# Revit family: bfs-15_150ska2_tka2_60Hz
name_source: partatom
category: 機械設備
units: mm (PartAtom-declared; Revit-internal decimal feet)

## family parameters
OmniClass タイトル = Centrifugal Fans
OmniClass 番号 = 23.75.35.17.27
パーツ タイプ = 割り込み
ロード時にボイドで切り取り = いいえ
丸型コネクタ寸法 = 直径を使用
作業面ベース = いいえ
共有 = いいえ
常に垂直 = はい
部屋計算ポイント = はい

## types (13) — shared parameters
Clearance Left = 450  [stored 1.47638 ft]
IfcExportAs = IfcFanType
IfcExportType = CENTRIFUGALFORWARDCURVED
MID静圧 = 0.0 Pa
MID風量 = 0.0 m³/h
OmniClassCode = 23-33 31 19 13 15
URL = https://www.mitsubishielectric.co.jp
Uniclass2015Code = Pr_65_67_29_12
Uniclass2015Title = Centrifugal fans
Uniclass2015Version = Systems v1.9
サービススペース = はい
ファンの種類 = 多翼形
仕様書バージョン = Version1.0
企業コード = 108420
分類コード = 50052502100020
周波数 = 60 Hz
呼称 = 消音ボックス付送風機
実風量 = 0.0 m³/h
形名 = BFS-SKA : BFS-15SKA
本体マテリアル = 溶融亜鉛めっき鋼板
極 = 4
法定耐用年数 = 15
盤工事区分 = 電気工事
積算_科目 = 2 換気設備
製品リリース年月 = 2022年6月1日
製品出荷対象 = 国内
製造元 = 三菱電機株式会社
設置方法 = 天吊
説明 = ストレートシロッコファン天吊埋込タイプ（高静圧形）
負荷分類 = 3_ファン類
運転質量 = 0.00 kg
zero-valued in all types: Clearance Back, Clearance Bottom, Clearance Front, Clearance Right, Clearance Top

## per-type parameters (varying)
| type | Depth | Height | M | MAX静圧 | MAX風量 | MIN静圧 | MIN風量 | Width | ダクト径 | 価格 | 天吊金具ピッチ奥行 | 天吊金具ピッチ幅 | 極数 | 消費電力 | 番手 | 相 | 製品質量 | 質量 | 電動機出力 | 電圧 | 騒音レベル(dB(A)) | 騒音レベル(dB(A))_側面 | 騒音レベル(dB(A))_吐出 | 騒音レベル(dB(A))_吸込 |
| BFS-15SKA2 | 335  [stored 1.09908 ft] | 226  [stored 0.74147 ft] | 60  [stored 0.19685 ft] | 80.0 Pa | 150.0 m³/h | 40.0 Pa | 105.0 m³/h | 223  [stored 0.731627 ft] | 100 mm | 49500 $ | 299  [stored 0.980971 ft] | 299  [stored 0.980971 ft] | 2 | 28 W | #1 | 1 | 5.20 kg | 6.24 kg | 8 W | 100 V | 38 | 24.5 | 38 | 33 |
| BFS-30SKA2 | 335  [stored 1.09908 ft] | 226  [stored 0.74147 ft] | 70  [stored 0.229659 ft] | 90.0 Pa | 300.0 m³/h | 40.0 Pa | 220.0 m³/h | 223  [stored 0.731627 ft] | 150 mm | 62000 $ | 299  [stored 0.980971 ft] | 299  [stored 0.980971 ft] | 2 | 62 W | #1 | 1 | 5.30 kg | 6.36 kg | 12 W | 100 V | 46 | 30 | 46 | 43 |
| BFS-40SKA2 | 389  [stored 1.27625 ft] | 255  [stored 0.836614 ft] | 70  [stored 0.229659 ft] | 110.0 Pa | 400.0 m³/h | 55.0 Pa | 280.0 m³/h | 255  [stored 0.836614 ft] | 150 mm | 73100 $ | 353  [stored 1.15814 ft] | 331  [stored 1.08596 ft] | 2 | 81 W | #1 1/4 | 1 | 7.00 kg | 8.40 kg | 30 W | 100 V | 48.5 | 31.5 | 48.5 | 43.5 |
| BFS-50SKA2 | 431  [stored 1.41404 ft] | 255  [stored 0.836614 ft] | 85  [stored 0.278871 ft] | 200.0 Pa | 500.0 m³/h | 125.0 Pa | 380.0 m³/h | 319  [stored 1.04659 ft] | 200 mm | 102000 $ | 395  [stored 1.29593 ft] | 395  [stored 1.29593 ft] | 2 | 102 W | #1 1/4 | 1 | 8.80 kg | 10.56 kg | 45 W | 100 V | 51.5 | 32 | 51.5 | 44.5 |
| BFS-65SKA2 | 489  [stored 1.60433 ft] | 305  [stored 1.00066 ft] | 85  [stored 0.278871 ft] | 220.0 Pa | 650.0 m³/h | 100.0 Pa | 460.0 m³/h | 373  [stored 1.22375 ft] | 200 mm | 108000 $ | 452  [stored 1.48294 ft] | 449  [stored 1.4731 ft] | 2 | 156 W | #1 1/4 | 1 | 11.10 kg | 13.32 kg | 75 W | 100 V | 53 | 33 | 53 | 45.5 |
| BFS-80SKA2 | 489  [stored 1.60433 ft] | 305  [stored 1.00066 ft] | 85  [stored 0.278871 ft] | 230.0 Pa | 800.0 m³/h | 140.0 Pa | 600.0 m³/h | 373  [stored 1.22375 ft] | 200 mm | 116000 $ | 452  [stored 1.48294 ft] | 449  [stored 1.4731 ft] | 2 | 203 W | #1 1/4 | 1 | 11.10 kg | 13.32 kg | 105 W | 100 V | 56 | 36 | 56 | 48 |
| BFS-100SKA2 | 528  [stored 1.73228 ft] | 350  [stored 1.14829 ft] | 85  [stored 0.278871 ft] | 310.0 Pa | 1000.0 m³/h | 200.0 Pa | 800.0 m³/h | 363  [stored 1.19094 ft] | 200 mm | 129000 $ | 492  [stored 1.61417 ft] | 440  [stored 1.44357 ft] | 2 | 356 W | #1 1/2 | 1 | 15.40 kg | 18.48 kg | 180 W | 100 V | 61 | 40.5 | 61 | 51 |
| BFS-120SKA2 | 591  [stored 1.93898 ft] | 350  [stored 1.14829 ft] | 85  [stored 0.278871 ft] | 330.0 Pa | 1200.0 m³/h | 175.0 Pa | 880.0 m³/h | 390  [stored 1.27953 ft] | 250 mm | 139000 $ | 554  [stored 1.81759 ft] | 467  [stored 1.53215 ft] | 2 | 388 W | #1 1/2 | 1 | 16.40 kg | 19.68 kg | 200 W | 100 V | 61.5 | 41 | 61.5 | 51.5 |
| BFS-150SKA2 | 591  [stored 1.93898 ft] | 350  [stored 1.14829 ft] | 85  [stored 0.278871 ft] | 350.0 Pa | 1500.0 m³/h | 235.0 Pa | 1220.0 m³/h | 390  [stored 1.27953 ft] | 250 mm | 149000 $ | 554  [stored 1.81759 ft] | 467  [stored 1.53215 ft] | 2 | 560 W | #1 1/2 | 1 | 16.60 kg | 19.92 kg | 300 W | 100 V | 63.5 | 44 | 63.5 | 55 |
| BFS-80TKA2 | 489  [stored 1.60433 ft] | 305  [stored 1.00066 ft] | 85  [stored 0.278871 ft] | 260.0 Pa | 800.0 m³/h | 145.0 Pa | 600.0 m³/h | 373  [stored 1.22375 ft] | 200 mm | 116000 $ | 452  [stored 1.48294 ft] | 449  [stored 1.4731 ft] | 3 | 190 W | #1 1/4 | 3 | 12.20 kg | 14.64 kg | 170 W | 200 V | 57 | 35 | 57 | 48 |
| BFS-100TKA2 | 528  [stored 1.73228 ft] | 350  [stored 1.14829 ft] | 85  [stored 0.278871 ft] | 320.0 Pa | 1000.0 m³/h | 140.0 Pa | 670.0 m³/h | 363  [stored 1.19094 ft] | 200 mm | 129000 $ | 492  [stored 1.61417 ft] | 440  [stored 1.44357 ft] | 3 | 326 W | #1 1/2 | 3 | 14.50 kg | 17.40 kg | 200 W | 200 V | 61.5 | 40.5 | 61.5 | 50.5 |
| BFS-120TKA2 | 591  [stored 1.93898 ft] | 350  [stored 1.14829 ft] | 85  [stored 0.278871 ft] | 370.0 Pa | 1200.0 m³/h | 175.0 Pa | 830.0 m³/h | 390  [stored 1.27953 ft] | 250 mm | 139000 $ | 554  [stored 1.81759 ft] | 467  [stored 1.53215 ft] | 3 | 397 W | #1 1/2 | 3 | 16.50 kg | 19.80 kg | 200 W | 200 V | 62 | 41 | 62 | 51.5 |
| BFS-150TKA2 | 591  [stored 1.93898 ft] | 350  [stored 1.14829 ft] | 85  [stored 0.278871 ft] | 370.0 Pa | 1500.0 m³/h | 200.0 Pa | 1110.0 m³/h | 390  [stored 1.27953 ft] | 250 mm | 149000 $ | 554  [stored 1.81759 ft] | 467  [stored 1.53215 ft] | 3 | 518 W | #1 1/2 | 3 | 16.50 kg | 19.80 kg | 300 W | 200 V | 63.5 | 42.5 | 63.5 | 55 |

note: column(s) folded — value = type name in every type: モデル

note: [stored X ft] marks values corroborated as IEEE doubles in the binary element streams (Revit-internal decimal feet)
